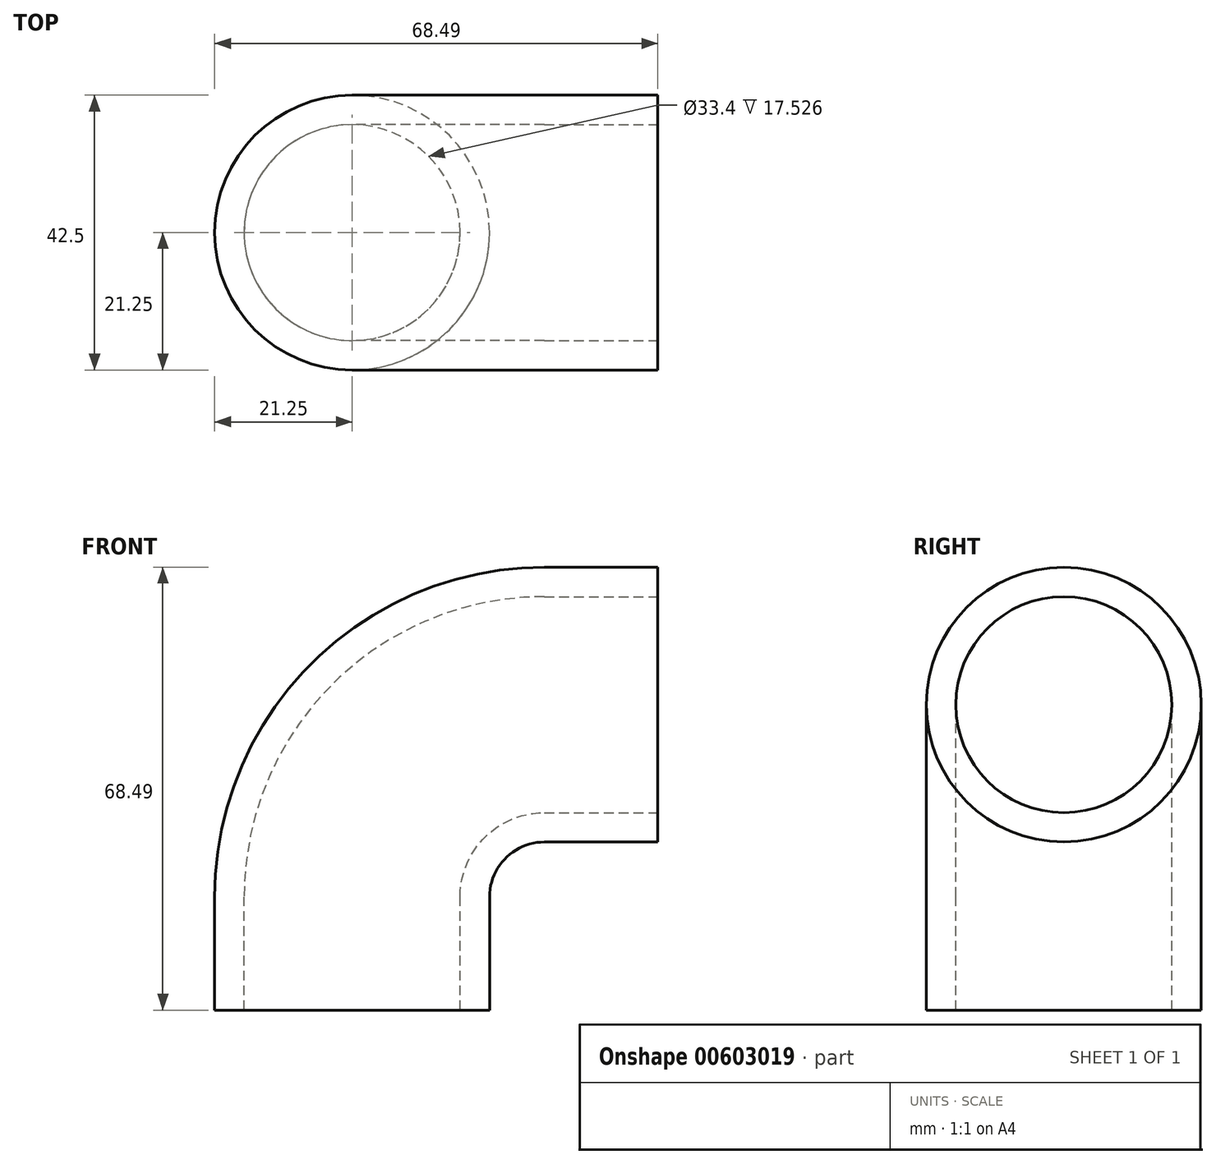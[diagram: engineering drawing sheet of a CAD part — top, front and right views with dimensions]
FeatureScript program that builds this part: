
annotation { "Feature Type Name" : "Feature", "Feature Type Description" : "" }
export const myFeature = defineFeature(function(context is Context, id is Id, definition is map)
    precondition{}
    {
        {
            var Q0;
            Q0=qCreatedBy(makeId("Top.planeOp"),FACE);
            var sketch = newSketch(context, id + "F0", { "sketchPlane" : qUnion([Q0])});
            skCircle(sketch, "E0", {"center": v(0, 0) * mm, "radius": 16.7 * mm});
            skCircle(sketch, "E1.0", {"center": v(0, 0) * mm, "radius": 21.25 * mm});
            skSolve(sketch);
        }
        {
            var Q0;
            Q0=qCreatedBy(makeId("Front.planeOp"),FACE);
            var sketch = newSketch(context, id + "F1", { "sketchPlane" : qUnion([Q0])});
            skLineSegment(sketch, "E2", {"start": v(0, 0) * mm, "end": v(0, 17.53) * mm});
            skLineSegment(sketch, "E3", {"start": v(29.72, 47.24) * mm, "end": v(47.24, 47.24) * mm});
            skPoint(sketch, "E4.visualSharp", {"position": v(0, 47.24) * mm});
            skArc(sketch, "E4.filletArc", {"start": v(29.72, 47.24) * mm, "mid": v(8.7, 38.54) * mm, "end": v(0, 17.53) * mm});
            skSolve(sketch);
        }
        {
            var Q0;
            Q0 = qSketchRegion(id + "F0", true);
            var Q1;
            Q1 = qConstructionFilter(qBodyType(qCreatedBy(id + "F1" ,EDGE), BodyType.WIRE), ConstructionObject.NO);
            sweep(context, id + "F2", {"profiles" : qUnion([Q0]), "path" : qUnion([Q1])});
        }
    });
